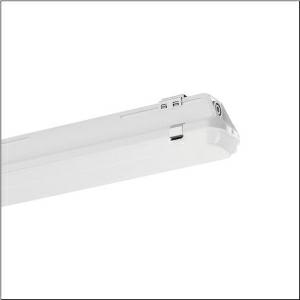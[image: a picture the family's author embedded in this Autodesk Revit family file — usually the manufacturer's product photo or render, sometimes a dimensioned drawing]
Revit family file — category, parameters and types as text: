
# Revit family: monsun_11_51fp208p430h
name_source: partatom
category: Lighting Fixtures
units: mm (PartAtom-declared; Revit-internal decimal feet)

## family parameters
Cut with Voids When Loaded = No
Host = Face
Light Source = No
Part Type = Normal
Room Calculation Point = No
Round Connector Dimension = Use Diameter
Shared = No

## types (1)
- Monsun 11 (1 x LED, 3990 lm, 24.8 W, 4000K)
    Apparent Load = 25 VA
    CIE Flux Codes = 45 75 93 94 100
    Color Rendering = 80
    Color Temperature = 4000K
    Default Elevation = 1800 mm
    Description = Monsun 11, damp-proof luminaire, chain hanger, primary optical cover: enclosure, of PC, light emission: direct distribution, primary light characteristic: symmetric, installation type: suspended mounting, surface-mounted, horizontal mounting, vertical mounting, LED, rated luminous flux: 3.990lm, luminous efficacy: 161lm/W, light colour: 840, colour temperature: 4000K, control gear: ON/OFF, with terminal, 3-pole, max. 2.5mm², mains connection: 220..240V, AC, 50/60Hz, rated input power: 25W, luminaire housing, of glass-fibre reinforced polyester, uncoated, bright grey, incl. chain hanger, length: 1.590mm, width: 90mm, height: 88mm, clip for enclosure, of stainless steel (V2A), ceiling mounting element, of stainless steel (V2A), chain hanger, of stainless steel (V2A), protection rating (complete): IP66, insulation class (complete): insulation class I (protective earthing), certification: CE, ENEC, VDE, UKCA, protection symbol: D, impact resistance: IK08, permissible operating ambient temperature: -35..+40°C, standard: EN 50419, EN 60598-2-1, no direct snow, no direct sun, no direct rain, for indoor or canopied outdoor use, corresponds to IFS (International Featured Standards) requirements for safety and quality in the food industry, contact your sales advisor before using the luminaires in applications with unclear chemical exposure, large temperature fluctuations or condensation-forming humidity, LABS conformity tested according to VDMA 24364:2018-05, packaging unit: 1 piece
    Height = 89 mm
    Lamp = 1 x LED
    Lamp Light Flux = 3990 lm
    Lamp Power = 24.8 W
    Lamp count = 1
    Length = 1590 mm
    Luminous efficacy = 161 lm/W
    Manufacturer = Siteco
    ModVariant = No
    Model = 51FP208P430H
    Mounting Place = Ceiling
    Mounting Type = Surface mounted
    Number of Poles = 1
    OnlyDefault = Yes
    Power Factor = 1
    Product Name = Monsun 11
    Product group = damp-proof luminaire
    ProductGroupID = 300
    Protection Class = Protection class I
    Protection Degree = IP 66
    RLX_Detail_Level = 1
    RLX_Emergency_Light_Flux = 0 lm
    RLX_Emergency_Type = 0
    RLX_Emergency_Type_DB = No
    RlxData = <blob elided: 88565 chars, md5=c2cac397>
    Socket = socket
    Standby Power = 0 W
    System Light Flux = 3990 lm
    System Power = 25 W
    Type Comments = Product without accessories
    Type Image = l_1349237.jpg
    URL = http://relux.com
    VarID = ---
    Voltage = 0 V
    Weight = 0.00 kg
    Width = 90 mm

## geometry (parser evidence)
native form markers: Blend x4, Sweep x14
no freeform markers — native parametric forms only
